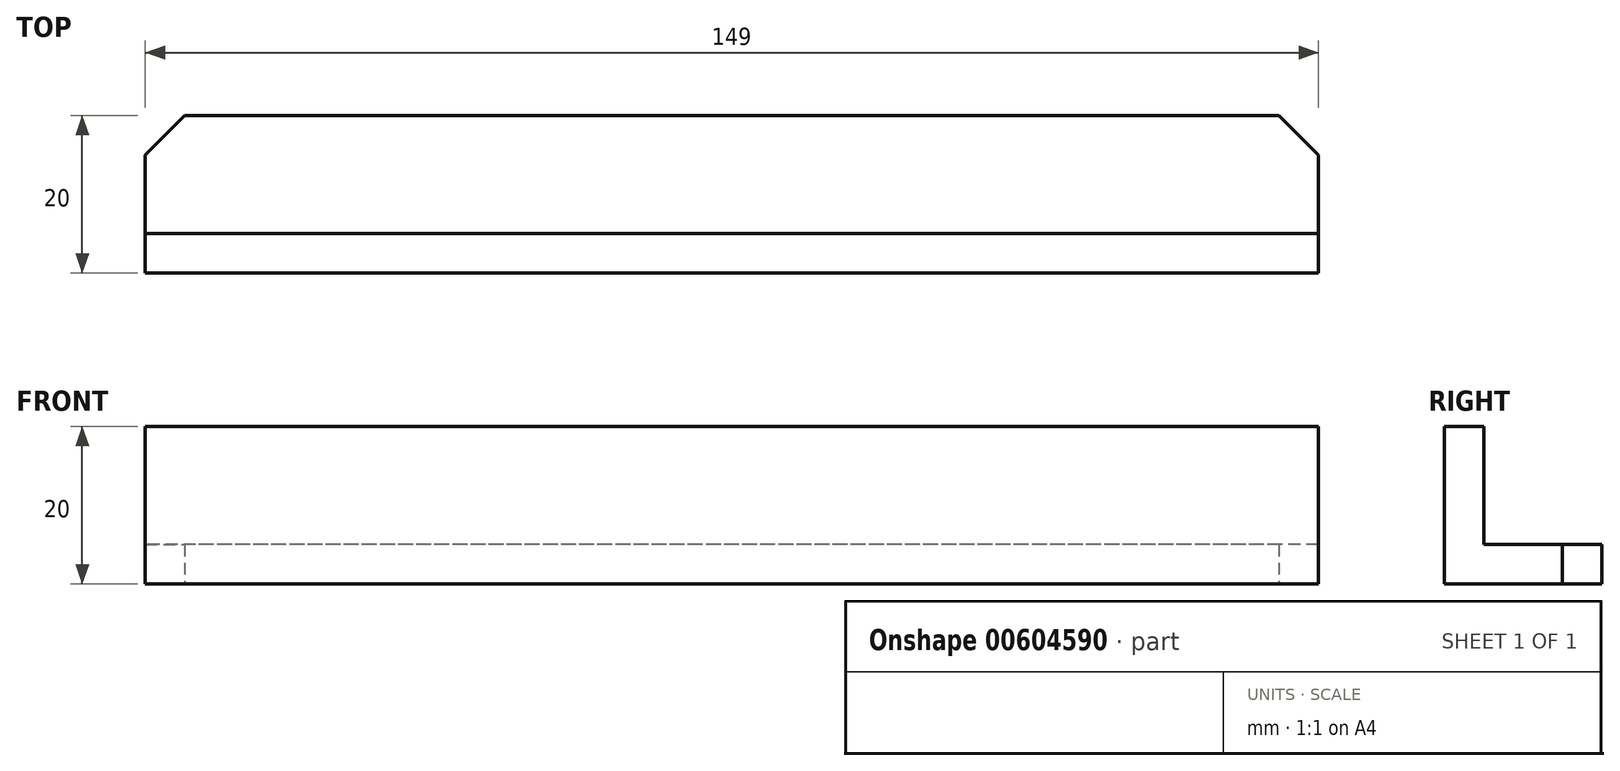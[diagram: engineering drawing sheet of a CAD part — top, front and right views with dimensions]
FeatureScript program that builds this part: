
annotation { "Feature Type Name" : "Feature", "Feature Type Description" : "" }
export const myFeature = defineFeature(function(context is Context, id is Id, definition is map)
    precondition{}
    {
        {
            var Q0;
            Q0=qCreatedBy(makeId("Right.planeOp"),FACE);
            var sketch = newSketch(context, id + "F0", { "sketchPlane" : qUnion([Q0])});
            skLineSegment(sketch, "E0", {"start": v(0, 0) * mm, "end": v(0, 20) * mm});
            skLineSegment(sketch, "E1", {"start": v(0, 20) * mm, "end": v(5, 20) * mm});
            skLineSegment(sketch, "E2", {"start": v(5, 20) * mm, "end": v(5, 5) * mm});
            skLineSegment(sketch, "E3", {"start": v(5, 5) * mm, "end": v(20, 5) * mm});
            skLineSegment(sketch, "E4", {"start": v(20, 5) * mm, "end": v(20, 0) * mm});
            skLineSegment(sketch, "E5", {"start": v(20, 0) * mm, "end": v(0, 0) * mm});
            skSolve(sketch);
        }
        {
            var Q0;
            Q0 = qSketchRegion(id + "F0", true);
            extrude(context, id + "F1", {"entities" : qUnion([Q0]), "depth" : 149 * mm, "offsetDistance" : 25 * mm});
        }
        {
            var Q0;
            Q0=qCreatedBy(makeId("Top.planeOp"),FACE);
            var sketch = newSketch(context, id + "F2", { "sketchPlane" : qUnion([Q0])});
            skLineSegment(sketch, "E6", {"start": v(0, 20) * mm, "end": v(0, 15) * mm});
            skLineSegment(sketch, "E7", {"start": v(0, 20) * mm, "end": v(5, 20) * mm});
            skLineSegment(sketch, "E8", {"start": v(5, 20) * mm, "end": v(0, 15) * mm});
            skLineSegment(sketch, "E9", {"start": v(149, 20) * mm, "end": v(149, 15) * mm});
            skLineSegment(sketch, "E10", {"start": v(149, 20) * mm, "end": v(144, 20) * mm});
            skLineSegment(sketch, "E11", {"start": v(144, 20) * mm, "end": v(149, 15) * mm});
            skSolve(sketch);
        }
        {
            var Q0;
            Q0 = qSketchRegion(id + "F2", true);
            extrude(context, id + "F3", {"entities" : qUnion([Q0]), "operationType" : NewBodyOperationType.REMOVE, "endBound" : BoundingType.THROUGH_ALL, "depth" : 25 * mm, "offsetDistance" : 25 * mm});
        }
    });
